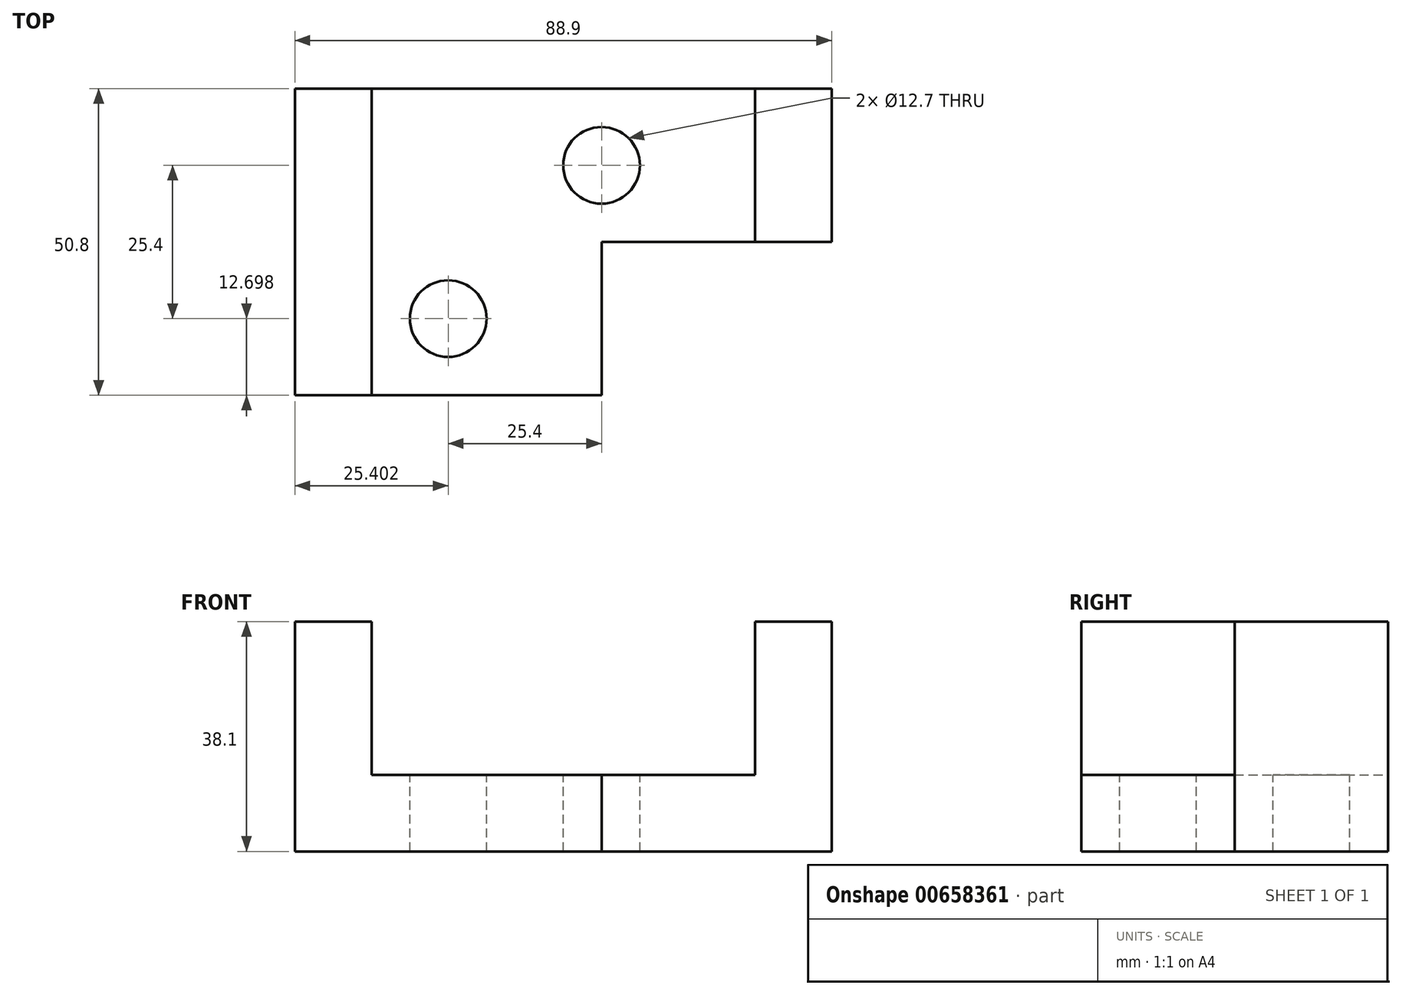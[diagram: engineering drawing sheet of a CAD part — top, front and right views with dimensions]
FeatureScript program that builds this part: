
annotation { "Feature Type Name" : "Feature", "Feature Type Description" : "" }
export const myFeature = defineFeature(function(context is Context, id is Id, definition is map)
    precondition{}
    {
        {
            var Q0;
            Q0=qCreatedBy(makeId("Top.planeOp"),FACE);
            var sketch = newSketch(context, id + "F0", { "sketchPlane" : qUnion([Q0])});
            skLineSegment(sketch, "E0", {"start": v(-50.16, 24.66) * mm, "end": v(-12.06, 24.66) * mm});
            skLineSegment(sketch, "E1", {"start": v(-12.06, 24.66) * mm, "end": v(-12.06, 50.06) * mm});
            skLineSegment(sketch, "E2", {"start": v(-12.06, 50.06) * mm, "end": v(26.04, 50.06) * mm});
            skLineSegment(sketch, "E3", {"start": v(26.04, 50.06) * mm, "end": v(26.04, 75.46) * mm});
            skLineSegment(sketch, "E4", {"start": v(26.04, 75.46) * mm, "end": v(-62.86, 75.46) * mm});
            skLineSegment(sketch, "E5", {"start": v(-62.86, 75.46) * mm, "end": v(-62.86, 24.66) * mm});
            skLineSegment(sketch, "E6", {"start": v(-62.86, 24.66) * mm, "end": v(-50.16, 24.66) * mm});
            skLineSegment(sketch, "E7", {"start": v(-50.16, 24.66) * mm, "end": v(-50.16, 75.46) * mm});
            skLineSegment(sketch, "E8", {"start": v(13.34, 50.06) * mm, "end": v(13.34, 75.46) * mm});
            skSolve(sketch);
        }
        {
            var Q0;
            {var subQ0=sQuery(id+"F0.wireOp",EDGE,"E5");Q0=makeQuery(id+"F0.imprint","IMPRINT",FACE,{"disambiguationData":[TD([[makeQuery(id+"F0.imprint","IMPRINT",EDGE,{"derivedFrom":subQ0}),1.0]])]});}
            var Q1;
            {var subQ1=sQuery(id+"F0.wireOp",EDGE,"E1");Q1=makeQuery(id+"F0.imprint","IMPRINT",FACE,{"disambiguationData":[TD([[makeQuery(id+"F0.imprint","IMPRINT",EDGE,{"derivedFrom":subQ1}),1.0]])]});}
            var Q2;
            {var subQ0=sQuery(id+"F0.wireOp",EDGE,"E3");Q2=makeQuery(id+"F0.imprint","IMPRINT",FACE,{"disambiguationData":[TD([[makeQuery(id+"F0.imprint","IMPRINT",EDGE,{"derivedFrom":subQ0}),1.0]])]});}
            extrude(context, id + "F1", {"entities" : qUnion([Q0, Q1, Q2]), "depth" : -12.7 * mm, "offsetDistance" : 25.4 * mm});
        }
        {
            var Q0;
            {var subQ0=sQuery(id+"F0.wireOp",EDGE,"E5");Q0=makeQuery(id+"F0.imprint","IMPRINT",FACE,{"disambiguationData":[TD([[makeQuery(id+"F0.imprint","IMPRINT",EDGE,{"derivedFrom":subQ0}),1.0]])]});}
            var Q1;
            {var subQ0=sQuery(id+"F0.wireOp",EDGE,"E3");Q1=makeQuery(id+"F0.imprint","IMPRINT",FACE,{"disambiguationData":[TD([[makeQuery(id+"F0.imprint","IMPRINT",EDGE,{"derivedFrom":subQ0}),1.0]])]});}
            extrude(context, id + "F2", {"entities" : qUnion([Q0, Q1]), "operationType" : NewBodyOperationType.ADD, "depth" : 25.4 * mm, "offsetDistance" : 25.4 * mm});
        }
        {
            var Q0;
            Q0=makeQuery(id+"F0.imprint","IMPRINT",FACE,{"disambiguationData":[TD([[makeQuery(id+"F0.imprint","IMPRINT",EDGE,{"derivedFrom":sQuery(id+"F0.wireOp",EDGE,"E0")}),1.0]])]});
            var sketch = newSketch(context, id + "F3", { "sketchPlane" : qUnion([Q0])});
            skCircle(sketch, "E9", {"center": v(-37.46, 37.36) * mm, "radius": 5.6 * mm});
            skCircle(sketch, "E10", {"center": v(-12.06, 62.76) * mm, "radius": 6.35 * mm});
            skSolve(sketch);
        }
        {
            var Q0;
            Q0=sQuery(id+"F3.wireOp",VERTEX,"E9.center");
            var Q1;
            Q1=sQuery(id+"F3.wireOp",VERTEX,"E10.center");
            var Q2;
            Q2=makeQuery(id+"F1.opExtrude","SWEPT_BODY",BODY,{"disambiguationData":[OSD([sQuery(id+"F0.wireOp",EDGE,"E0"),sQuery(id+"F0.wireOp",EDGE,"E1"),sQuery(id+"F0.wireOp",EDGE,"E2"),sQuery(id+"F0.wireOp",EDGE,"E3"),sQuery(id+"F0.wireOp",EDGE,"E4"),sQuery(id+"F0.wireOp",EDGE,"E5"),sQuery(id+"F0.wireOp",EDGE,"E6")])]});
            hole(context, id + "F4", {"style" : HoleStyle.SIMPLE, "endStyle" : HoleEndStyle.THROUGH, "holeDiameter" : 12.7 * mm, "majorDiameter" : 6.35 * mm, "isTappedThrough" : true, "tappedDepth" : 12.7 * mm, "tapClearance" : 3, "locations" : qUnion([Q0, Q1]), "scope" : qUnion([Q2])});
        }
    });
